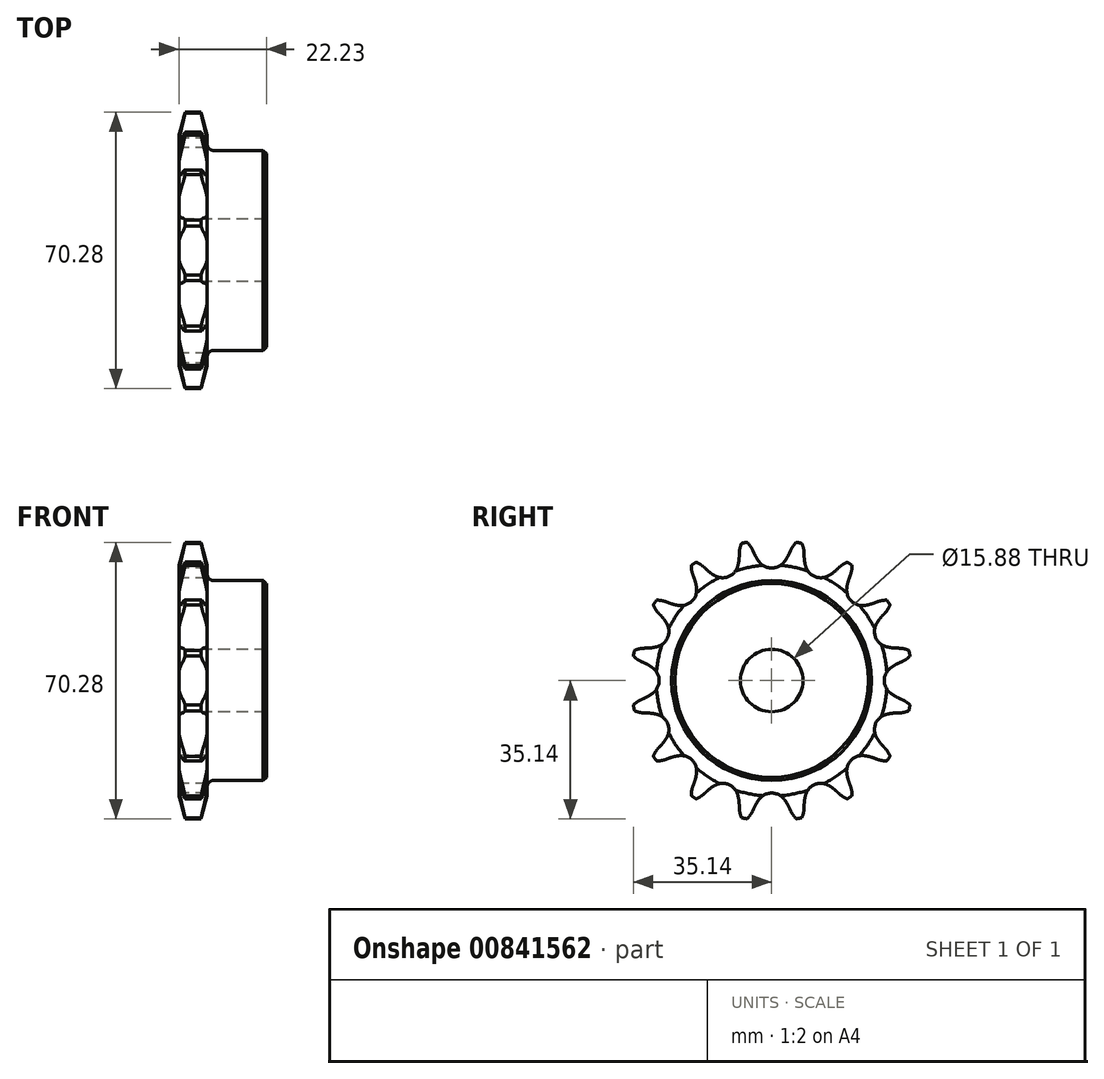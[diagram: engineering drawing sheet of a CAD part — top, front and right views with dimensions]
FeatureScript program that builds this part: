
annotation { "Feature Type Name" : "Feature", "Feature Type Description" : "" }
export const myFeature = defineFeature(function(context is Context, id is Id, definition is map)
    precondition{}
    {
        {
            var Q0;
            Q0=qCreatedBy(makeId("Front.planeOp"),FACE);
            var sketch = newSketch(context, id + "F0", { "sketchPlane" : qUnion([Q0])});
            skLineSegment(sketch, "E0", {"start": v(0, 0) * mm, "end": v(48.72, 0) * mm, "construction": true});
            skLineSegment(sketch, "E1.bottom", {"start": v(0, 35.69) * mm, "end": v(7.21, 35.69) * mm});
            skLineSegment(sketch, "E1.top", {"start": v(0, 7.94) * mm, "end": v(7.21, 7.94) * mm});
            skLineSegment(sketch, "E1.left", {"start": v(0, 35.69) * mm, "end": v(0, 7.94) * mm});
            skLineSegment(sketch, "E1.right", {"start": v(7.21, 35.69) * mm, "end": v(7.21, 7.94) * mm});
            skLineSegment(sketch, "E2.bottom", {"start": v(0, 7.94) * mm, "end": v(22.23, 7.94) * mm});
            skLineSegment(sketch, "E2.top", {"start": v(0, 25.4) * mm, "end": v(22.23, 25.4) * mm});
            skLineSegment(sketch, "E2.left", {"start": v(0, 7.94) * mm, "end": v(0, 25.4) * mm});
            skLineSegment(sketch, "E2.right", {"start": v(22.23, 7.94) * mm, "end": v(22.23, 25.4) * mm});
            skLineSegment(sketch, "E3.MirrorCS", {"start": v(0, -7.94) * mm, "end": v(7.21, -7.94) * mm});
            skLineSegment(sketch, "E4.MirrorCS", {"start": v(22.23, -7.94) * mm, "end": v(22.23, -25.4) * mm});
            skLineSegment(sketch, "E5.MirrorCS", {"start": v(0, -7.94) * mm, "end": v(22.23, -7.94) * mm});
            skLineSegment(sketch, "E6.MirrorCS", {"start": v(0, -35.69) * mm, "end": v(7.21, -35.69) * mm});
            skLineSegment(sketch, "E7.MirrorCS", {"start": v(0, -7.94) * mm, "end": v(0, -25.4) * mm});
            skLineSegment(sketch, "E8.MirrorCS", {"start": v(7.21, -35.69) * mm, "end": v(7.21, -7.94) * mm});
            skLineSegment(sketch, "E9.MirrorCS", {"start": v(0, -25.4) * mm, "end": v(22.23, -25.4) * mm});
            skLineSegment(sketch, "E10.MirrorCS", {"start": v(0, -35.69) * mm, "end": v(0, -7.94) * mm});
            skSolve(sketch);
        }
        {
            var Q0;
            {var subQ0=sQuery(id+"F0.wireOp",EDGE,"E1.bottom");Q0=makeQuery(id+"F0.imprint","IMPRINT",FACE,{"disambiguationData":[TD([[makeQuery(id+"F0.imprint","IMPRINT",EDGE,{"derivedFrom":subQ0}),-1.0]])]});}
            var Q1;
            {var subQ0=sQuery(id+"F0.wireOp",EDGE,"E1.top");Q1=makeQuery(id+"F0.imprint","IMPRINT",FACE,{"disambiguationData":[TD([[makeQuery(id+"F0.imprint","IMPRINT",EDGE,{"derivedFrom":subQ0}),1.0]])]});}
            var Q2;
            {var subQ0=sQuery(id+"F0.wireOp",EDGE,"E2.bottom");Q2=makeQuery(id+"F0.imprint","IMPRINT",FACE,{"disambiguationData":[TD([[makeQuery(id+"F0.imprint","IMPRINT",EDGE,{"derivedFrom":subQ0}),1.0]])]});}
            var Q3;
            Q3=sQuery(id+"F0.wireOp",EDGE,"E0");
            revolve(context, id + "F1", {"surfaceOperationType" : NewSurfaceOperationType.NEW, "entities" : qUnion([Q0, Q1, Q2]), "axis" : qUnion([Q3]), "revolveType" : RevolveType.FULL});
        }
        {
            var Q0;
            Q0=makeQuery(id+"F1.opRevolve","SWEPT_EDGE",EDGE,{"disambiguationData":[OSD([sQuery(id+"F0.wireOp",EDGE,"E1.right"),sQuery(id+"F0.wireOp",EDGE,"E2.top")])]});
            fillet(context, id + "F2", {"entities" : qUnion([Q0]), "radius" : 1.59 * mm, "tangentPropagation" : true, "allowEdgeOverflow" : false});
        }
        {
            var Q0;
            Q0=makeQuery(id+"F1.opRevolve","SWEPT_EDGE",EDGE,{"disambiguationData":[OSD([sQuery(id+"F0.wireOp",EDGE,"E2.top"),sQuery(id+"F0.wireOp",EDGE,"E2.right")])]});
            chamfer(context, id + "F3", {"entities" : qUnion([Q0]), "width" : 0.8 * mm, "tangentPropagation" : true});
        }
        {
            var Q0;
            Q0=makeQuery(id+"F1.opRevolve","SWEPT_EDGE",EDGE,{"disambiguationData":[OSD([sQuery(id+"F0.wireOp",EDGE,"E1.bottom"),sQuery(id+"F0.wireOp",EDGE,"E1.left")])]});
            var Q1;
            Q1=makeQuery(id+"F1.opRevolve","SWEPT_EDGE",EDGE,{"disambiguationData":[OSD([sQuery(id+"F0.wireOp",EDGE,"E1.bottom"),sQuery(id+"F0.wireOp",EDGE,"E1.right")])]});
            chamfer(context, id + "F4", {"entities" : qUnion([Q0, Q1]), "chamferType" : ChamferType.TWO_OFFSETS, "width1" : 6.35 * mm, "oppositeDirection" : false, "width2" : 1.59 * mm, "tangentPropagation" : true});
        }
        {
            var Q0;
            Q0=makeQuery(id+"F1.opRevolve","SWEPT_FACE",FACE,{"disambiguationData":[OSD([sQuery(id+"F0.wireOp",EDGE,"E1.left")])]});
            var sketch = newSketch(context, id + "F5", { "sketchPlane" : qUnion([Q0])});
            skCircle(sketch, "E11", {"center": v(0, 0) * mm, "radius": 32.55 * mm, "construction": true});
            skLineSegment(sketch, "E12", {"start": v(0, 0) * mm, "end": v(0, 32.55) * mm, "construction": true});
            skLineSegment(sketch, "E13", {"start": v(0, 32.55) * mm, "end": v(19.26, 32.55) * mm, "construction": true});
            skLineSegment(sketch, "E14", {"start": v(0, 32.55) * mm, "end": v(5, 36.56) * mm, "construction": true});
            skLineSegment(sketch, "E15", {"start": v(5, 36.56) * mm, "end": v(-4.46, 32.3) * mm, "construction": true});
            skLineSegment(sketch, "E16", {"start": v(-4.46, 32.3) * mm, "end": v(-4.82, 33.1) * mm});
            skLineSegment(sketch, "E17", {"start": v(0, 0) * mm, "end": v(-7.13, 35.85) * mm, "construction": true});
            skArc(sketch, "E18", {"start": v(-7.13, 35.85) * mm, "mid": v(-15.87, 26.15) * mm, "end": v(-4.82, 33.1) * mm, "construction": true});
            skArc(sketch, "E19", {"start": v(-4.82, 33.1) * mm, "mid": v(-5.78, 34.63) * mm, "end": v(-7.13, 35.85) * mm});
            skLineSegment(sketch, "E20", {"start": v(-4.82, 33.1) * mm, "end": v(-4.82, 33.1) * mm});
            skLineSegment(sketch, "E21", {"start": v(-4.46, 32.3) * mm, "end": v(-4.46, 32.3) * mm});
            skArc(sketch, "E22", {"start": v(-4.46, 32.3) * mm, "mid": v(-3.84, 31.14) * mm, "end": v(-3.1, 30.07) * mm});
            skArc(sketch, "E23", {"start": v(-3.1, 30.07) * mm, "mid": v(13.83, 41.97) * mm, "end": v(-4.46, 32.3) * mm, "construction": true});
            skLineSegment(sketch, "E24", {"start": v(-0.09, 22.6) * mm, "end": v(-4.82, 33.1) * mm, "construction": true});
            skArc(sketch, "E25.MirrorCS", {"start": v(4.46, 32.3) * mm, "mid": v(3.84, 31.14) * mm, "end": v(3.1, 30.07) * mm});
            skLineSegment(sketch, "E26.MirrorCS", {"start": v(4.46, 32.3) * mm, "end": v(4.82, 33.1) * mm});
            skArc(sketch, "E27.MirrorCS", {"start": v(4.82, 33.1) * mm, "mid": v(5.78, 34.63) * mm, "end": v(7.13, 35.85) * mm});
            skArc(sketch, "E28", {"start": v(3.1, 30.07) * mm, "mid": v(0, 36.51) * mm, "end": v(-3.1, 30.07) * mm, "construction": true});
            skArc(sketch, "E29", {"start": v(-3.1, 30.07) * mm, "mid": v(0, 28.59) * mm, "end": v(3.1, 30.07) * mm});
            skArc(sketch, "E30.1.0", {"start": v(-17.12, 28.74) * mm, "mid": v(-18.6, 29.79) * mm, "end": v(-20.3, 30.4) * mm});
            skLineSegment(sketch, "E30.1.1", {"start": v(-16.48, 28.14) * mm, "end": v(-17.12, 28.74) * mm});
            skArc(sketch, "E30.1.2", {"start": v(-16.48, 28.14) * mm, "mid": v(-15.47, 27.3) * mm, "end": v(-14.36, 26.6) * mm});
            skArc(sketch, "E30.1.3", {"start": v(-14.36, 26.6) * mm, "mid": v(-10.94, 26.41) * mm, "end": v(-8.65, 28.96) * mm});
            skArc(sketch, "E30.1.4", {"start": v(-8.24, 31.55) * mm, "mid": v(-8.37, 30.24) * mm, "end": v(-8.65, 28.96) * mm});
            skLineSegment(sketch, "E30.1.5", {"start": v(-8.24, 31.55) * mm, "end": v(-8.22, 32.42) * mm});
            skArc(sketch, "E30.1.6", {"start": v(-8.22, 32.42) * mm, "mid": v(-7.91, 34.21) * mm, "end": v(-7.13, 35.85) * mm});
            skArc(sketch, "E30.2.0", {"start": v(-26.8, 20) * mm, "mid": v(-28.58, 20.4) * mm, "end": v(-30.4, 20.3) * mm});
            skLineSegment(sketch, "E30.2.1", {"start": v(-26, 19.69) * mm, "end": v(-26.8, 20) * mm});
            skArc(sketch, "E30.2.2", {"start": v(-26, 19.69) * mm, "mid": v(-24.74, 19.3) * mm, "end": v(-23.45, 19.08) * mm});
            skArc(sketch, "E30.2.3", {"start": v(-23.45, 19.08) * mm, "mid": v(-20.21, 20.21) * mm, "end": v(-19.08, 23.45) * mm});
            skArc(sketch, "E30.2.4", {"start": v(-19.69, 26) * mm, "mid": v(-19.3, 24.74) * mm, "end": v(-19.08, 23.45) * mm});
            skLineSegment(sketch, "E30.2.5", {"start": v(-19.69, 26) * mm, "end": v(-20, 26.8) * mm});
            skArc(sketch, "E30.2.6", {"start": v(-20, 26.8) * mm, "mid": v(-20.4, 28.58) * mm, "end": v(-20.3, 30.4) * mm});
            skArc(sketch, "E30.3.0", {"start": v(-32.42, 8.22) * mm, "mid": v(-34.21, 7.91) * mm, "end": v(-35.85, 7.13) * mm});
            skLineSegment(sketch, "E30.3.1", {"start": v(-31.55, 8.24) * mm, "end": v(-32.42, 8.22) * mm});
            skArc(sketch, "E30.3.2", {"start": v(-31.55, 8.24) * mm, "mid": v(-30.24, 8.37) * mm, "end": v(-28.96, 8.65) * mm});
            skArc(sketch, "E30.3.3", {"start": v(-28.96, 8.65) * mm, "mid": v(-26.41, 10.94) * mm, "end": v(-26.6, 14.36) * mm});
            skArc(sketch, "E30.3.4", {"start": v(-28.14, 16.48) * mm, "mid": v(-27.3, 15.47) * mm, "end": v(-26.6, 14.36) * mm});
            skLineSegment(sketch, "E30.3.5", {"start": v(-28.14, 16.48) * mm, "end": v(-28.74, 17.12) * mm});
            skArc(sketch, "E30.3.6", {"start": v(-28.74, 17.12) * mm, "mid": v(-29.79, 18.6) * mm, "end": v(-30.4, 20.3) * mm});
            skArc(sketch, "E30.4.0", {"start": v(-33.1, -4.82) * mm, "mid": v(-34.63, -5.78) * mm, "end": v(-35.85, -7.13) * mm});
            skLineSegment(sketch, "E30.4.1", {"start": v(-32.3, -4.46) * mm, "end": v(-33.1, -4.82) * mm});
            skArc(sketch, "E30.4.2", {"start": v(-32.3, -4.46) * mm, "mid": v(-31.14, -3.84) * mm, "end": v(-30.07, -3.1) * mm});
            skArc(sketch, "E30.4.3", {"start": v(-30.07, -3.1) * mm, "mid": v(-28.59, 0) * mm, "end": v(-30.07, 3.1) * mm});
            skArc(sketch, "E30.4.4", {"start": v(-32.3, 4.46) * mm, "mid": v(-31.14, 3.84) * mm, "end": v(-30.07, 3.1) * mm});
            skLineSegment(sketch, "E30.4.5", {"start": v(-32.3, 4.46) * mm, "end": v(-33.1, 4.82) * mm});
            skArc(sketch, "E30.4.6", {"start": v(-33.1, 4.82) * mm, "mid": v(-34.63, 5.78) * mm, "end": v(-35.85, 7.13) * mm});
            skArc(sketch, "E30.5.0", {"start": v(-28.74, -17.12) * mm, "mid": v(-29.79, -18.6) * mm, "end": v(-30.4, -20.3) * mm});
            skLineSegment(sketch, "E30.5.1", {"start": v(-28.14, -16.48) * mm, "end": v(-28.74, -17.12) * mm});
            skArc(sketch, "E30.5.2", {"start": v(-28.14, -16.48) * mm, "mid": v(-27.3, -15.47) * mm, "end": v(-26.6, -14.36) * mm});
            skArc(sketch, "E30.5.3", {"start": v(-26.6, -14.36) * mm, "mid": v(-26.41, -10.94) * mm, "end": v(-28.96, -8.65) * mm});
            skArc(sketch, "E30.5.4", {"start": v(-31.55, -8.24) * mm, "mid": v(-30.24, -8.37) * mm, "end": v(-28.96, -8.65) * mm});
            skLineSegment(sketch, "E30.5.5", {"start": v(-31.55, -8.24) * mm, "end": v(-32.42, -8.22) * mm});
            skArc(sketch, "E30.5.6", {"start": v(-32.42, -8.22) * mm, "mid": v(-34.21, -7.91) * mm, "end": v(-35.85, -7.13) * mm});
            skArc(sketch, "E30.6.0", {"start": v(-20, -26.8) * mm, "mid": v(-20.4, -28.58) * mm, "end": v(-20.3, -30.4) * mm});
            skLineSegment(sketch, "E30.6.1", {"start": v(-19.69, -26) * mm, "end": v(-20, -26.8) * mm});
            skArc(sketch, "E30.6.2", {"start": v(-19.69, -26) * mm, "mid": v(-19.3, -24.74) * mm, "end": v(-19.08, -23.45) * mm});
            skArc(sketch, "E30.6.3", {"start": v(-19.08, -23.45) * mm, "mid": v(-20.21, -20.21) * mm, "end": v(-23.45, -19.08) * mm});
            skArc(sketch, "E30.6.4", {"start": v(-26, -19.69) * mm, "mid": v(-24.74, -19.3) * mm, "end": v(-23.45, -19.08) * mm});
            skLineSegment(sketch, "E30.6.5", {"start": v(-26, -19.69) * mm, "end": v(-26.8, -20) * mm});
            skArc(sketch, "E30.6.6", {"start": v(-26.8, -20) * mm, "mid": v(-28.58, -20.4) * mm, "end": v(-30.4, -20.3) * mm});
            skArc(sketch, "E30.7.0", {"start": v(-8.22, -32.42) * mm, "mid": v(-7.91, -34.21) * mm, "end": v(-7.13, -35.85) * mm});
            skLineSegment(sketch, "E30.7.1", {"start": v(-8.24, -31.55) * mm, "end": v(-8.22, -32.42) * mm});
            skArc(sketch, "E30.7.2", {"start": v(-8.24, -31.55) * mm, "mid": v(-8.37, -30.24) * mm, "end": v(-8.65, -28.96) * mm});
            skArc(sketch, "E30.7.3", {"start": v(-8.65, -28.96) * mm, "mid": v(-10.94, -26.41) * mm, "end": v(-14.36, -26.6) * mm});
            skArc(sketch, "E30.7.4", {"start": v(-16.48, -28.14) * mm, "mid": v(-15.47, -27.3) * mm, "end": v(-14.36, -26.6) * mm});
            skLineSegment(sketch, "E30.7.5", {"start": v(-16.48, -28.14) * mm, "end": v(-17.12, -28.74) * mm});
            skArc(sketch, "E30.7.6", {"start": v(-17.12, -28.74) * mm, "mid": v(-18.6, -29.79) * mm, "end": v(-20.3, -30.4) * mm});
            skArc(sketch, "E30.8.0", {"start": v(4.82, -33.1) * mm, "mid": v(5.78, -34.63) * mm, "end": v(7.13, -35.85) * mm});
            skLineSegment(sketch, "E30.8.1", {"start": v(4.46, -32.3) * mm, "end": v(4.82, -33.1) * mm});
            skArc(sketch, "E30.8.2", {"start": v(4.46, -32.3) * mm, "mid": v(3.84, -31.14) * mm, "end": v(3.1, -30.07) * mm});
            skArc(sketch, "E30.8.3", {"start": v(3.1, -30.07) * mm, "mid": v(0, -28.59) * mm, "end": v(-3.1, -30.07) * mm});
            skArc(sketch, "E30.8.4", {"start": v(-4.46, -32.3) * mm, "mid": v(-3.84, -31.14) * mm, "end": v(-3.1, -30.07) * mm});
            skLineSegment(sketch, "E30.8.5", {"start": v(-4.46, -32.3) * mm, "end": v(-4.82, -33.1) * mm});
            skArc(sketch, "E30.8.6", {"start": v(-4.82, -33.1) * mm, "mid": v(-5.78, -34.63) * mm, "end": v(-7.13, -35.85) * mm});
            skArc(sketch, "E30.9.0", {"start": v(17.12, -28.74) * mm, "mid": v(18.6, -29.79) * mm, "end": v(20.3, -30.4) * mm});
            skLineSegment(sketch, "E30.9.1", {"start": v(16.48, -28.14) * mm, "end": v(17.12, -28.74) * mm});
            skArc(sketch, "E30.9.2", {"start": v(16.48, -28.14) * mm, "mid": v(15.47, -27.3) * mm, "end": v(14.36, -26.6) * mm});
            skArc(sketch, "E30.9.3", {"start": v(14.36, -26.6) * mm, "mid": v(10.94, -26.41) * mm, "end": v(8.65, -28.96) * mm});
            skArc(sketch, "E30.9.4", {"start": v(8.24, -31.55) * mm, "mid": v(8.37, -30.24) * mm, "end": v(8.65, -28.96) * mm});
            skLineSegment(sketch, "E30.9.5", {"start": v(8.24, -31.55) * mm, "end": v(8.22, -32.42) * mm});
            skArc(sketch, "E30.9.6", {"start": v(8.22, -32.42) * mm, "mid": v(7.91, -34.21) * mm, "end": v(7.13, -35.85) * mm});
            skArc(sketch, "E30.10.0", {"start": v(26.8, -20) * mm, "mid": v(28.58, -20.4) * mm, "end": v(30.4, -20.3) * mm});
            skLineSegment(sketch, "E30.10.1", {"start": v(26, -19.69) * mm, "end": v(26.8, -20) * mm});
            skArc(sketch, "E30.10.2", {"start": v(26, -19.69) * mm, "mid": v(24.74, -19.3) * mm, "end": v(23.45, -19.08) * mm});
            skArc(sketch, "E30.10.3", {"start": v(23.45, -19.08) * mm, "mid": v(20.21, -20.21) * mm, "end": v(19.08, -23.45) * mm});
            skArc(sketch, "E30.10.4", {"start": v(19.69, -26) * mm, "mid": v(19.3, -24.74) * mm, "end": v(19.08, -23.45) * mm});
            skLineSegment(sketch, "E30.10.5", {"start": v(19.69, -26) * mm, "end": v(20, -26.8) * mm});
            skArc(sketch, "E30.10.6", {"start": v(20, -26.8) * mm, "mid": v(20.4, -28.58) * mm, "end": v(20.3, -30.4) * mm});
            skArc(sketch, "E30.11.0", {"start": v(32.42, -8.22) * mm, "mid": v(34.21, -7.91) * mm, "end": v(35.85, -7.13) * mm});
            skLineSegment(sketch, "E30.11.1", {"start": v(31.55, -8.24) * mm, "end": v(32.42, -8.22) * mm});
            skArc(sketch, "E30.11.2", {"start": v(31.55, -8.24) * mm, "mid": v(30.24, -8.37) * mm, "end": v(28.96, -8.65) * mm});
            skArc(sketch, "E30.11.3", {"start": v(28.96, -8.65) * mm, "mid": v(26.41, -10.94) * mm, "end": v(26.6, -14.36) * mm});
            skArc(sketch, "E30.11.4", {"start": v(28.14, -16.48) * mm, "mid": v(27.3, -15.47) * mm, "end": v(26.6, -14.36) * mm});
            skLineSegment(sketch, "E30.11.5", {"start": v(28.14, -16.48) * mm, "end": v(28.74, -17.12) * mm});
            skArc(sketch, "E30.11.6", {"start": v(28.74, -17.12) * mm, "mid": v(29.79, -18.6) * mm, "end": v(30.4, -20.3) * mm});
            skArc(sketch, "E30.12.0", {"start": v(33.1, 4.82) * mm, "mid": v(34.63, 5.78) * mm, "end": v(35.85, 7.13) * mm});
            skLineSegment(sketch, "E30.12.1", {"start": v(32.3, 4.46) * mm, "end": v(33.1, 4.82) * mm});
            skArc(sketch, "E30.12.2", {"start": v(32.3, 4.46) * mm, "mid": v(31.14, 3.84) * mm, "end": v(30.07, 3.1) * mm});
            skArc(sketch, "E30.12.3", {"start": v(30.07, 3.1) * mm, "mid": v(28.59, 0) * mm, "end": v(30.07, -3.1) * mm});
            skArc(sketch, "E30.12.4", {"start": v(32.3, -4.46) * mm, "mid": v(31.14, -3.84) * mm, "end": v(30.07, -3.1) * mm});
            skLineSegment(sketch, "E30.12.5", {"start": v(32.3, -4.46) * mm, "end": v(33.1, -4.82) * mm});
            skArc(sketch, "E30.12.6", {"start": v(33.1, -4.82) * mm, "mid": v(34.63, -5.78) * mm, "end": v(35.85, -7.13) * mm});
            skArc(sketch, "E30.13.0", {"start": v(28.74, 17.12) * mm, "mid": v(29.79, 18.6) * mm, "end": v(30.4, 20.3) * mm});
            skLineSegment(sketch, "E30.13.1", {"start": v(28.14, 16.48) * mm, "end": v(28.74, 17.12) * mm});
            skArc(sketch, "E30.13.2", {"start": v(28.14, 16.48) * mm, "mid": v(27.3, 15.47) * mm, "end": v(26.6, 14.36) * mm});
            skArc(sketch, "E30.13.3", {"start": v(26.6, 14.36) * mm, "mid": v(26.41, 10.94) * mm, "end": v(28.96, 8.65) * mm});
            skArc(sketch, "E30.13.4", {"start": v(31.55, 8.24) * mm, "mid": v(30.24, 8.37) * mm, "end": v(28.96, 8.65) * mm});
            skLineSegment(sketch, "E30.13.5", {"start": v(31.55, 8.24) * mm, "end": v(32.42, 8.22) * mm});
            skArc(sketch, "E30.13.6", {"start": v(32.42, 8.22) * mm, "mid": v(34.21, 7.91) * mm, "end": v(35.85, 7.13) * mm});
            skArc(sketch, "E30.14.0", {"start": v(20, 26.8) * mm, "mid": v(20.4, 28.58) * mm, "end": v(20.3, 30.4) * mm});
            skLineSegment(sketch, "E30.14.1", {"start": v(19.69, 26) * mm, "end": v(20, 26.8) * mm});
            skArc(sketch, "E30.14.2", {"start": v(19.69, 26) * mm, "mid": v(19.3, 24.74) * mm, "end": v(19.08, 23.45) * mm});
            skArc(sketch, "E30.14.3", {"start": v(19.08, 23.45) * mm, "mid": v(20.21, 20.21) * mm, "end": v(23.45, 19.08) * mm});
            skArc(sketch, "E30.14.4", {"start": v(26, 19.69) * mm, "mid": v(24.74, 19.3) * mm, "end": v(23.45, 19.08) * mm});
            skLineSegment(sketch, "E30.14.5", {"start": v(26, 19.69) * mm, "end": v(26.8, 20) * mm});
            skArc(sketch, "E30.14.6", {"start": v(26.8, 20) * mm, "mid": v(28.58, 20.4) * mm, "end": v(30.4, 20.3) * mm});
            skArc(sketch, "E30.15.0", {"start": v(8.22, 32.42) * mm, "mid": v(7.91, 34.21) * mm, "end": v(7.13, 35.85) * mm});
            skLineSegment(sketch, "E30.15.1", {"start": v(8.24, 31.55) * mm, "end": v(8.22, 32.42) * mm});
            skArc(sketch, "E30.15.2", {"start": v(8.24, 31.55) * mm, "mid": v(8.37, 30.24) * mm, "end": v(8.65, 28.96) * mm});
            skArc(sketch, "E30.15.3", {"start": v(8.65, 28.96) * mm, "mid": v(10.94, 26.41) * mm, "end": v(14.36, 26.6) * mm});
            skArc(sketch, "E30.15.4", {"start": v(16.48, 28.14) * mm, "mid": v(15.47, 27.3) * mm, "end": v(14.36, 26.6) * mm});
            skLineSegment(sketch, "E30.15.5", {"start": v(16.48, 28.14) * mm, "end": v(17.12, 28.74) * mm});
            skArc(sketch, "E30.15.6", {"start": v(17.12, 28.74) * mm, "mid": v(18.6, 29.79) * mm, "end": v(20.3, 30.4) * mm});
            skSolve(sketch);
        }
        {
            var Q0;
            Q0 = qSketchRegion(id + "F5", true);
            extrude(context, id + "F6", {"entities" : qUnion([Q0]), "operationType" : NewBodyOperationType.INTERSECT, "endBound" : BoundingType.THROUGH_ALL, "oppositeDirection" : true, "depth" : 25.4 * mm, "offsetDistance" : 25.4 * mm});
        }
    });
